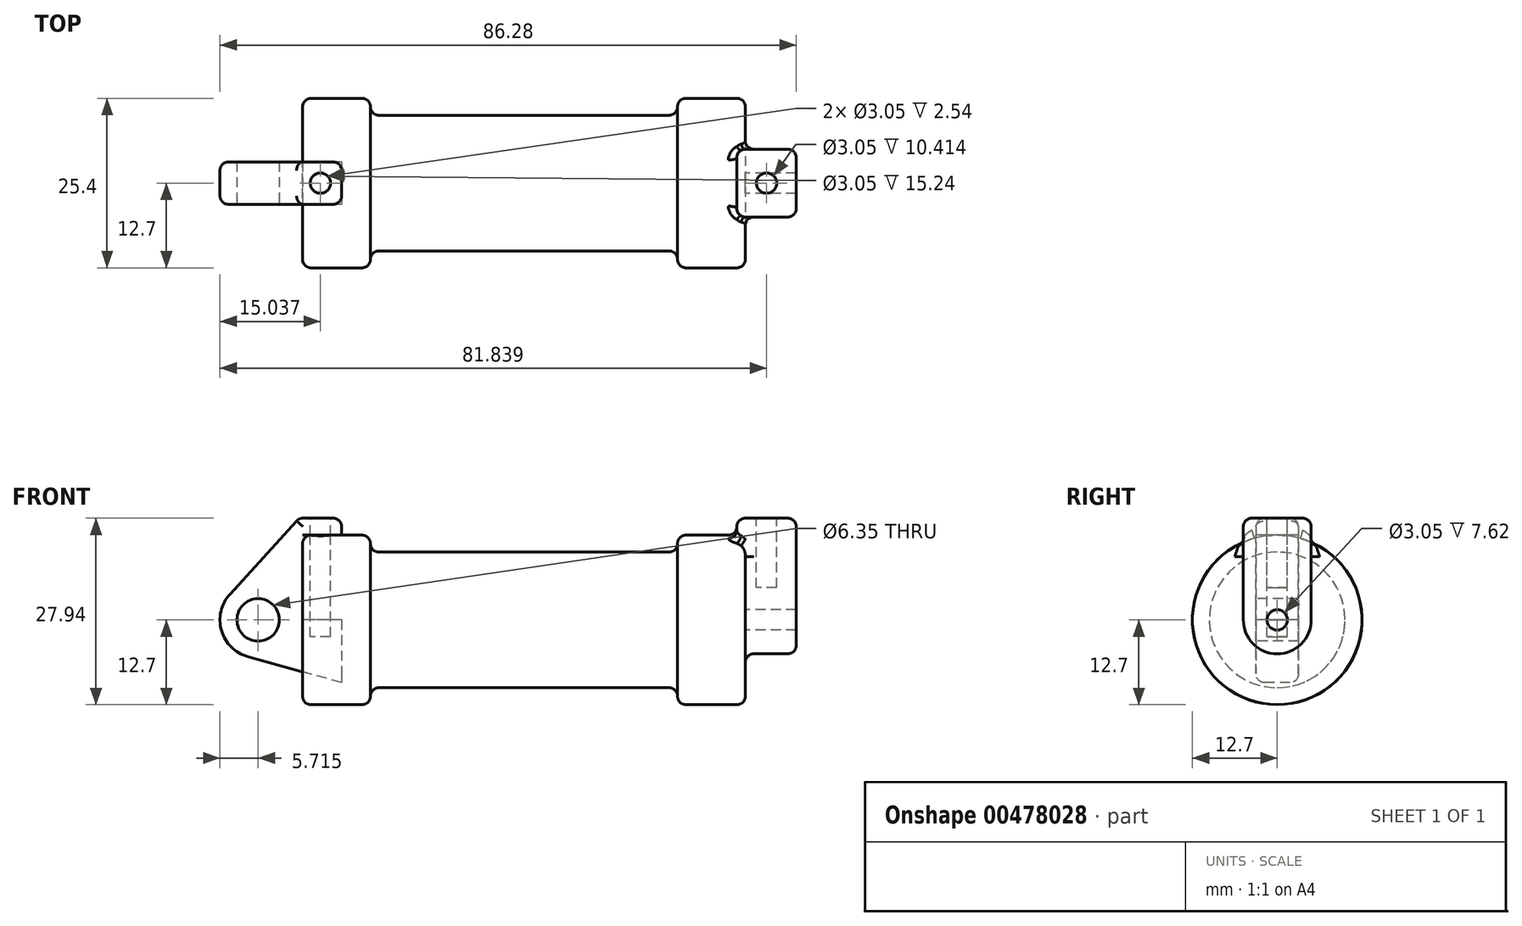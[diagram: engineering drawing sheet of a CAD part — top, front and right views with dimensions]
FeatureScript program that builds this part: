
annotation { "Feature Type Name" : "Feature", "Feature Type Description" : "" }
export const myFeature = defineFeature(function(context is Context, id is Id, definition is map)
    precondition{}
    {
        {
            var Q0;
            Q0=qCreatedBy(makeId("Front.planeOp"),FACE);
            var sketch = newSketch(context, id + "F0", { "sketchPlane" : qUnion([Q0])});
            skLineSegment(sketch, "E0", {"start": v(0, 0) * mm, "end": v(0, 12.7) * mm});
            skLineSegment(sketch, "E1", {"start": v(0, 12.7) * mm, "end": v(10.16, 12.7) * mm});
            skLineSegment(sketch, "E2", {"start": v(10.16, 12.7) * mm, "end": v(10.16, 10.16) * mm});
            skLineSegment(sketch, "E3", {"start": v(10.16, 10.16) * mm, "end": v(56.13, 10.16) * mm});
            skLineSegment(sketch, "E4", {"start": v(56.13, 10.16) * mm, "end": v(56.13, 12.7) * mm});
            skLineSegment(sketch, "E5", {"start": v(56.13, 12.7) * mm, "end": v(66.3, 12.7) * mm});
            skLineSegment(sketch, "E6", {"start": v(66.3, 12.7) * mm, "end": v(66.3, 0) * mm});
            skLineSegment(sketch, "E7", {"start": v(66.3, 0) * mm, "end": v(0, 0) * mm});
            skLineSegment(sketch, "E8", {"start": v(5.84, 15.24) * mm, "end": v(-0.5, 15.24) * mm});
            skLineSegment(sketch, "E9", {"start": v(-0.5, 15.24) * mm, "end": v(-10.88, 3.85) * mm});
            skLineSegment(sketch, "E10", {"start": v(0, 0) * mm, "end": v(-6.65, 0) * mm});
            skCircle(sketch, "E11", {"center": v(-6.65, 0) * mm, "radius": 5.72 * mm});
            skCircle(sketch, "E12", {"center": v(-6.65, 0) * mm, "radius": 3.18 * mm});
            skLineSegment(sketch, "E13", {"start": v(5.84, 15.24) * mm, "end": v(5.84, -9.4) * mm});
            skLineSegment(sketch, "E14", {"start": v(5.84, -9.4) * mm, "end": v(-8.18, -5.5) * mm});
            skSolve(sketch);
        }
        {
            var Q0;
            {var subQ1=sQuery(id+"F0.wireOp",EDGE,"E0");Q0=makeQuery(id+"F0.imprint","IMPRINT",FACE,{"disambiguationData":[TD([[makeQuery(id+"F0.imprint","IMPRINT",EDGE,{"derivedFrom":subQ1}),1.0]])]});}
            var Q1;
            {var subQ0=sQuery(id+"F0.wireOp",EDGE,"E14");Q1=makeQuery(id+"F0.imprint","IMPRINT",FACE,{"disambiguationData":[TD([[makeQuery(id+"F0.imprint","IMPRINT",EDGE,{"derivedFrom":subQ0}),-1.0]])]});}
            var Q2;
            {var subQ5=sQuery(id+"F0.wireOp",EDGE,"E12");Q2=makeQuery(id+"F0.imprint","IMPRINT",FACE,{"disambiguationData":[TD([[makeQuery(id+"F0.imprint","IMPRINT",EDGE,{"derivedFrom":subQ5}),-1.0]])]});}
            extrude(context, id + "F1", {"entities" : qUnion([Q0, Q1, Q2]), "endBound" : BoundingType.SYMMETRIC, "oppositeDirection" : true, "depth" : 6.35 * mm});
        }
        {
            var Q0;
            {var subQ0=sQuery(id+"F0.wireOp",EDGE,"E2");Q0=makeQuery(id+"F0.imprint","IMPRINT",FACE,{"disambiguationData":[TD([[makeQuery(id+"F0.imprint","IMPRINT",EDGE,{"derivedFrom":subQ0}),-1.0]])]});}
            var Q1;
            {var subQ0=sQuery(id+"F0.wireOp",EDGE,"E0");Q1=makeQuery(id+"F0.imprint","IMPRINT",FACE,{"disambiguationData":[TD([[makeQuery(id+"F0.imprint","IMPRINT",EDGE,{"derivedFrom":subQ0}),-1.0]])]});}
            var Q2;
            Q2=sQuery(id+"F0.wireOp",EDGE,"E7");
            revolve(context, id + "F2", {"entities" : qUnion([Q0, Q1]), "axis" : qUnion([Q2]), "revolveType" : RevolveType.FULL});
        }
        {
            var Q0;
            Q0=makeQuery(id+"F2.opRevolve","SWEPT_FACE",FACE,{"disambiguationData":[OSD([sQuery(id+"F0.wireOp",EDGE,"E6")])]});
            var sketch = newSketch(context, id + "F3", { "sketchPlane" : qUnion([Q0])});
            skCircle(sketch, "E15", {"center": v(0, 0) * mm, "radius": 1.52 * mm});
            skCircle(sketch, "E16", {"center": v(0, 0) * mm, "radius": 5.08 * mm});
            skLineSegment(sketch, "E17", {"start": v(5.08, 0) * mm, "end": v(5.08, 15.24) * mm});
            skLineSegment(sketch, "E18", {"start": v(5.08, 15.24) * mm, "end": v(-5.08, 15.24) * mm});
            skLineSegment(sketch, "E19", {"start": v(-5.08, 15.24) * mm, "end": v(-5.08, 0) * mm});
            skSolve(sketch);
        }
        {
            var Q0;
            Q0=makeQuery(id+"F3.imprint","IMPRINT",FACE,{"disambiguationData":[TD([[makeQuery(id+"F3.imprint","IMPRINT",EDGE,{"derivedFrom":sQuery(id+"F3.wireOp",EDGE,"E15")}),-1.0]])]});
            var Q1;
            {var subQ0=sQuery(id+"F3.wireOp",EDGE,"E17");var subQ1=sQuery(id+"F3.wireOp",EDGE,"E16");var subQ2=makeQuery(id+"F3.imprint","INTERSECT",VERTEX,{"derivedFrom":[subQ1,subQ0]});Q1=makeQuery(id+"F3.imprint","IMPRINT",FACE,{"disambiguationData":[TD([[makeQuery(id+"F3.imprint","IMPRINT",EDGE,{"disambiguationData":[TD([[subQ2,-1.0]])],"derivedFrom":subQ1}),-1.0]])]});}
            var Q2;
            {var subQ0=sQuery(id+"F3.wireOp",EDGE,"E18");Q2=makeQuery(id+"F3.imprint","IMPRINT",FACE,{"disambiguationData":[TD([[makeQuery(id+"F3.imprint","IMPRINT",EDGE,{"derivedFrom":subQ0}),1.0]])]});}
            extrude(context, id + "F4", {"entities" : qUnion([Q0, Q1, Q2]), "operationType" : NewBodyOperationType.ADD, "depth" : 7.62 * mm, "hasSecondDirection" : true, "secondDirectionOppositeDirection" : true, "secondDirectionDepth" : 1.27 * mm});
        }
        {
            var Q0;
            Q0=makeQuery(id+"F4.opExtrude","SWEPT_FACE",FACE,{"disambiguationData":[OSD([sQuery(id+"F3.wireOp",EDGE,"E18")])]});
            var sketch = newSketch(context, id + "F5", { "sketchPlane" : qUnion([Q0])});
            skPoint(sketch, "E20.centerSnap0", {"position": v(65.02, 0) * mm});
            skCircle(sketch, "E21", {"center": v(69.47, 0) * mm, "radius": 1.52 * mm});
            skSolve(sketch);
        }
        {
            var Q0;
            Q0=makeQuery(id+"F1.opExtrude","SWEPT_FACE",FACE,{"disambiguationData":[OSD([sQuery(id+"F0.wireOp",EDGE,"E8")])]});
            var sketch = newSketch(context, id + "F6", { "sketchPlane" : qUnion([Q0])});
            skCircle(sketch, "E22", {"center": v(2.67, 0) * mm, "radius": 1.52 * mm});
            skSolve(sketch);
        }
        {
            var Q0;
            Q0=makeQuery(id+"F5.imprint","IMPRINT",FACE,{"disambiguationData":[TD([[makeQuery(id+"F5.imprint","IMPRINT",EDGE,{"derivedFrom":sQuery(id+"F5.wireOp",EDGE,"E21")}),1.0]])]});
            extrude(context, id + "F7", {"entities" : qUnion([Q0]), "operationType" : NewBodyOperationType.REMOVE, "oppositeDirection" : true, "depth" : 10.4 * mm});
        }
        {
            var Q0;
            Q0=makeQuery(id+"F6.imprint","IMPRINT",FACE,{"disambiguationData":[TD([[makeQuery(id+"F6.imprint","IMPRINT",EDGE,{"derivedFrom":sQuery(id+"F6.wireOp",EDGE,"E22")}),1.0]])]});
            extrude(context, id + "F8", {"entities" : qUnion([Q0]), "operationType" : NewBodyOperationType.REMOVE, "oppositeDirection" : true, "depth" : 17.78 * mm});
        }
        {
            var Q0;
            Q0=makeQuery(id+"F2.opRevolve","SWEPT_EDGE",EDGE,{"disambiguationData":[OSD([sQuery(id+"F0.wireOp",EDGE,"E4"),sQuery(id+"F0.wireOp",EDGE,"E5")])]});
            fillet(context, id + "F9", {"entities" : qUnion([Q0]), "radius" : 1.27 * mm, "tangentPropagation" : true, "allowEdgeOverflow" : false});
        }
        {
            var Q0;
            Q0=makeQuery(id+"F2.opRevolve","SWEPT_EDGE",EDGE,{"disambiguationData":[OSD([sQuery(id+"F0.wireOp",EDGE,"E1"),sQuery(id+"F0.wireOp",EDGE,"E2")])]});
            var Q1;
            Q1=makeQuery(id+"F2.opRevolve","SWEPT_EDGE",EDGE,{"disambiguationData":[OSD([sQuery(id+"F0.wireOp",EDGE,"E0"),sQuery(id+"F0.wireOp",EDGE,"E1")])]});
            fillet(context, id + "F10", {"entities" : qUnion([Q0, Q1]), "radius" : 1.27 * mm, "tangentPropagation" : true, "allowEdgeOverflow" : false});
        }
        {
            var Q0;
            Q0=makeQuery(id+"F2.opRevolve","SWEPT_EDGE",EDGE,{"disambiguationData":[OSD([sQuery(id+"F0.wireOp",EDGE,"E5"),sQuery(id+"F0.wireOp",EDGE,"E6")])]});
            fillet(context, id + "F11", {"entities" : qUnion([Q0]), "radius" : 1.27 * mm, "tangentPropagation" : true, "allowEdgeOverflow" : false});
        }
        {
            var Q0;
            Q0=makeQuery(id+"F1.opExtrude","CAP_EDGE",EDGE,{"disambiguationData":[OSD([sQuery(id+"F0.wireOp",EDGE,"E9")])],"isStart":true});
            var Q1;
            Q1=makeQuery(id+"F1.opExtrude","CAP_EDGE",EDGE,{"disambiguationData":[OSD([sQuery(id+"F0.wireOp",EDGE,"E9")])],"isStart":false});
            var Q2;
            Q2=makeQuery(id+"F1.opExtrude","CAP_EDGE",EDGE,{"disambiguationData":[OSD([sQuery(id+"F0.wireOp",EDGE,"E11")])],"isStart":false});
            var Q3;
            Q3=makeQuery(id+"F1.opExtrude","CAP_EDGE",EDGE,{"disambiguationData":[OSD([sQuery(id+"F0.wireOp",EDGE,"E11")])],"isStart":true});
            var Q4;
            Q4=makeQuery(id+"F1.opExtrude","CAP_EDGE",EDGE,{"disambiguationData":[OSD([sQuery(id+"F0.wireOp",EDGE,"E14")])],"isStart":false});
            var Q5;
            Q5=makeQuery(id+"F1.opExtrude","CAP_EDGE",EDGE,{"disambiguationData":[OSD([sQuery(id+"F0.wireOp",EDGE,"E14")])],"isStart":true});
            var Q6;
            Q6=makeQuery(id+"F1.opExtrude","CAP_EDGE",EDGE,{"disambiguationData":[OSD([sQuery(id+"F0.wireOp",EDGE,"E8")])],"isStart":true});
            var Q7;
            Q7=makeQuery(id+"F1.opExtrude","CAP_EDGE",EDGE,{"disambiguationData":[OSD([sQuery(id+"F0.wireOp",EDGE,"E8")])],"isStart":false});
            var Q8;
            Q8=makeQuery(id+"F1.opExtrude","SWEPT_EDGE",EDGE,{"disambiguationData":[OSD([sQuery(id+"F0.wireOp",EDGE,"E8"),sQuery(id+"F0.wireOp",EDGE,"E13")])]});
            var Q9;
            {var subQ0=sQuery(id+"F0.wireOp",EDGE,"E13");Q9=makeQuery(id+"F1.opExtrude","CAP_EDGE",EDGE,{"disambiguationData":[OSD([subQ0]),TDD([makeQuery(id+"F0.imprint","IMPRINT",EDGE,{"disambiguationData":[TD([[makeQuery(id+"F0.imprint","INTERSECT",VERTEX,{"derivedFrom":[sQuery(id+"F0.wireOp",EDGE,"E8"),subQ0]}),-1.0]])],"derivedFrom":subQ0})])],"isStart":true});}
            var Q10;
            {var subQ0=sQuery(id+"F0.wireOp",EDGE,"E13");Q10=makeQuery(id+"F1.opExtrude","CAP_EDGE",EDGE,{"disambiguationData":[OSD([subQ0]),TDD([makeQuery(id+"F0.imprint","IMPRINT",EDGE,{"disambiguationData":[TD([[makeQuery(id+"F0.imprint","INTERSECT",VERTEX,{"derivedFrom":[sQuery(id+"F0.wireOp",EDGE,"E8"),subQ0]}),-1.0]])],"derivedFrom":subQ0})])],"isStart":false});}
            fillet(context, id + "F12", {"entities" : qUnion([Q0, Q1, Q2, Q3, Q4, Q5, Q6, Q7, Q8, Q9, Q10]), "radius" : 1.27 * mm, "tangentPropagation" : true, "allowEdgeOverflow" : false});
        }
        {
            var Q0;
            Q0=makeQuery(id+"F2.opRevolve","SWEPT_EDGE",EDGE,{"disambiguationData":[OSD([sQuery(id+"F0.wireOp",EDGE,"E3"),sQuery(id+"F0.wireOp",EDGE,"E4")])]});
            fillet(context, id + "F13", {"entities" : qUnion([Q0]), "radius" : 1.27 * mm, "tangentPropagation" : true, "allowEdgeOverflow" : false});
        }
        {
            var Q0;
            Q0=makeQuery(id+"F2.opRevolve","SWEPT_EDGE",EDGE,{"disambiguationData":[OSD([sQuery(id+"F0.wireOp",EDGE,"E2"),sQuery(id+"F0.wireOp",EDGE,"E3")])]});
            fillet(context, id + "F14", {"entities" : qUnion([Q0]), "radius" : 1.27 * mm, "tangentPropagation" : true, "allowEdgeOverflow" : false});
        }
        {
            var Q0;
            Q0=makeQuery(id+"F4.opExtrude","CAP_EDGE",EDGE,{"disambiguationData":[OSD([sQuery(id+"F3.wireOp",EDGE,"E17")])],"isStart":false});
            var Q1;
            Q1=makeQuery(id+"F4.opExtrude","CAP_EDGE",EDGE,{"disambiguationData":[OSD([sQuery(id+"F3.wireOp",EDGE,"E18")])],"isStart":false});
            var Q2;
            Q2=makeQuery(id+"F4.opExtrude","SWEPT_EDGE",EDGE,{"disambiguationData":[OSD([sQuery(id+"F3.wireOp",EDGE,"E17"),sQuery(id+"F3.wireOp",EDGE,"E18")])]});
            var Q3;
            Q3=makeQuery(id+"F4.opExtrude","CAP_EDGE",EDGE,{"disambiguationData":[OSD([sQuery(id+"F3.wireOp",EDGE,"E16")])],"isStart":false});
            var Q4;
            Q4=makeQuery(id+"F4.opExtrude","CAP_EDGE",EDGE,{"disambiguationData":[OSD([sQuery(id+"F3.wireOp",EDGE,"E19")])],"isStart":false});
            var Q5;
            Q5=makeQuery(id+"F4.opExtrude","SWEPT_EDGE",EDGE,{"disambiguationData":[OSD([sQuery(id+"F3.wireOp",EDGE,"E18"),sQuery(id+"F3.wireOp",EDGE,"E19")])]});
            var Q6;
            Q6=makeQuery(id+"F4.opExtrude","CAP_EDGE",EDGE,{"disambiguationData":[OSD([sQuery(id+"F3.wireOp",EDGE,"E18")])],"isStart":true});
            var Q7;
            Q7=makeQuery(id+"F4.opExtrude","CAP_EDGE",EDGE,{"disambiguationData":[OSD([sQuery(id+"F3.wireOp",EDGE,"E19")])],"isStart":true});
            var Q8;
            Q8=makeQuery(id+"F4.opExtrude","CAP_EDGE",EDGE,{"disambiguationData":[OSD([sQuery(id+"F3.wireOp",EDGE,"E17")])],"isStart":true});
            fillet(context, id + "F15", {"entities" : qUnion([Q0, Q1, Q2, Q3, Q4, Q5, Q6, Q7, Q8]), "radius" : 1.27 * mm, "tangentPropagation" : true, "allowEdgeOverflow" : false});
        }
        {
            var Q0;
            Q0=makeQuery(id+"F4.boolean.opBoolean","INTERSECT",EDGE,{"derivedFrom":[makeQuery(id+"F2.opRevolve","SWEPT_FACE",FACE,{"disambiguationData":[OSD([sQuery(id+"F0.wireOp",EDGE,"E6")])]}),makeQuery(id+"F4.opExtrude","SWEPT_FACE",FACE,{"disambiguationData":[OSD([sQuery(id+"F3.wireOp",EDGE,"E19")])]})]});
            var Q1;
            Q1=makeQuery(id+"F4.boolean.opBoolean","INTERSECT",EDGE,{"derivedFrom":[makeQuery(id+"F2.opRevolve","SWEPT_FACE",FACE,{"disambiguationData":[OSD([sQuery(id+"F0.wireOp",EDGE,"E6")])]}),makeQuery(id+"F4.opExtrude","SWEPT_FACE",FACE,{"disambiguationData":[OSD([sQuery(id+"F3.wireOp",EDGE,"E16")])]})]});
            var Q2;
            Q2=makeQuery(id+"F4.boolean.opBoolean","INTERSECT",EDGE,{"derivedFrom":[makeQuery(id+"F2.opRevolve","SWEPT_FACE",FACE,{"disambiguationData":[OSD([sQuery(id+"F0.wireOp",EDGE,"E6")])]}),makeQuery(id+"F4.opExtrude","SWEPT_FACE",FACE,{"disambiguationData":[OSD([sQuery(id+"F3.wireOp",EDGE,"E17")])]})]});
            var Q3;
            Q3=makeQuery(id+"F4.boolean.opBoolean","INTERSECT",EDGE,{"derivedFrom":[makeQuery(id+"F2.opRevolve","SWEPT_FACE",FACE,{"disambiguationData":[OSD([sQuery(id+"F0.wireOp",EDGE,"E5")])]}),makeQuery(id+"F4.opExtrude","CAP_FACE",FACE,{"disambiguationData":[OSD([sQuery(id+"F3.wireOp",EDGE,"E15"),sQuery(id+"F3.wireOp",EDGE,"E16"),sQuery(id+"F3.wireOp",EDGE,"E17"),sQuery(id+"F3.wireOp",EDGE,"E18"),sQuery(id+"F3.wireOp",EDGE,"E19")])],"isStart":true})]});
            fillet(context, id + "F16", {"entities" : qUnion([Q0, Q1, Q2, Q3]), "radius" : 1.27 * mm, "tangentPropagation" : true, "allowEdgeOverflow" : false});
        }
        {
            var Q0;
            Q0=makeQuery(id+"F1.opExtrude","SWEPT_EDGE",EDGE,{"disambiguationData":[OSD([sQuery(id+"F0.wireOp",EDGE,"E8"),sQuery(id+"F0.wireOp",EDGE,"E9")])]});
            fillet(context, id + "F17", {"entities" : qUnion([Q0]), "radius" : 1.27 * mm, "tangentPropagation" : true, "allowEdgeOverflow" : false});
        }
    });
